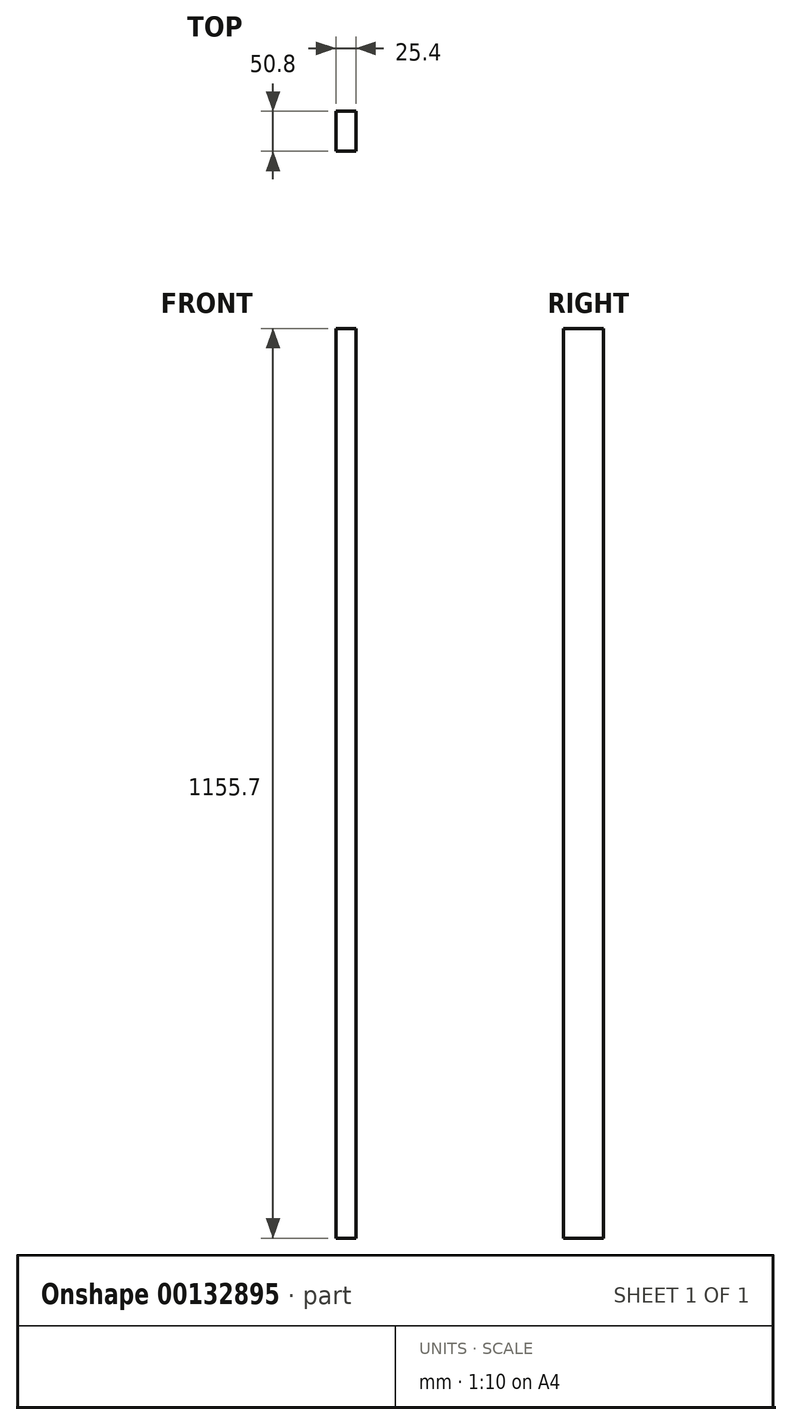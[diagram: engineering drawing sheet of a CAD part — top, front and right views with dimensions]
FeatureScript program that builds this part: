
annotation { "Feature Type Name" : "Feature", "Feature Type Description" : "" }
export const myFeature = defineFeature(function(context is Context, id is Id, definition is map)
    precondition{}
    {
        {
            var Q0;
            Q0=qCreatedBy(makeId("Right.planeOp"),FACE);
            var sketch = newSketch(context, id + "F0", { "sketchPlane" : qUnion([Q0])});
            skLineSegment(sketch, "E0.bottom", {"start": v(-35.48, 1051.46) * mm, "end": v(15.32, 1051.46) * mm});
            skLineSegment(sketch, "E0.top", {"start": v(-35.48, -104.24) * mm, "end": v(15.32, -104.24) * mm});
            skLineSegment(sketch, "E0.left", {"start": v(-35.48, 1051.46) * mm, "end": v(-35.48, -104.24) * mm});
            skLineSegment(sketch, "E0.right", {"start": v(15.32, 1051.46) * mm, "end": v(15.32, -104.24) * mm});
            skSolve(sketch);
        }
        {
            var Q0;
            Q0=makeQuery(id+"F0.imprint","IMPRINT",FACE,{"disambiguationData":[TD([[makeQuery(id+"F0.imprint","IMPRINT",EDGE,{"derivedFrom":sQuery(id+"F0.wireOp",EDGE,"E0.bottom")}),-1.0]])]});
            extrude(context, id + "F1", {"entities" : qUnion([Q0]), "depth" : 25.4 * mm});
        }
    });
